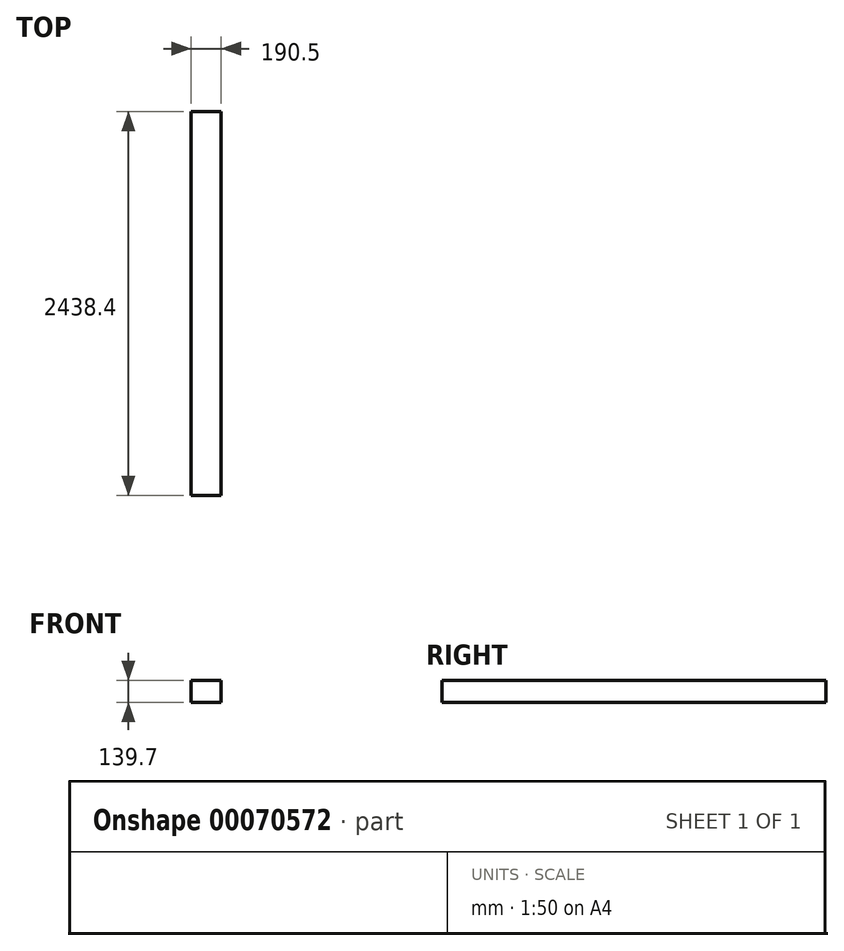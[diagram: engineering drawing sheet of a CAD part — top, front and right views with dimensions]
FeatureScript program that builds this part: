
annotation { "Feature Type Name" : "Feature", "Feature Type Description" : "" }
export const myFeature = defineFeature(function(context is Context, id is Id, definition is map)
    precondition{}
    {
        {
            var Q0;
            Q0=qCreatedBy(makeId("Front.planeOp"),FACE);
            var sketch = newSketch(context, id + "F0", { "sketchPlane" : qUnion([Q0])});
            skLineSegment(sketch, "E0.rect.bottom", {"start": v(95.25, 69.85) * mm, "end": v(-95.25, 69.85) * mm});
            skLineSegment(sketch, "E0.rect.top", {"start": v(95.25, -69.85) * mm, "end": v(-95.25, -69.85) * mm});
            skLineSegment(sketch, "E0.rect.left", {"start": v(95.25, 69.85) * mm, "end": v(95.25, -69.85) * mm});
            skLineSegment(sketch, "E0.rect.right", {"start": v(-95.25, 69.85) * mm, "end": v(-95.25, -69.85) * mm});
            skPoint(sketch, "E0.rect.middle", {"position": v(0, 0) * mm});
            skSolve(sketch);
        }
        {
            var Q0;
            Q0=makeQuery(id+"F0.imprint","IMPRINT",FACE,{"disambiguationData":[TD([[makeQuery(id+"F0.imprint","IMPRINT",EDGE,{"derivedFrom":sQuery(id+"F0.wireOp",EDGE,"E0.rect.bottom")}),1.0]])]});
            extrude(context, id + "F1", {"entities" : qUnion([Q0]), "oppositeDirection" : true, "depth" : 2438.4 * mm});
        }
    });
